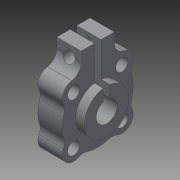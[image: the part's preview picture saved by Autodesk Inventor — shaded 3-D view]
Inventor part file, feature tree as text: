
AUTODESK INVENTOR PART (.ipt)
format: ipt  version: 2014 SP1 (Build 180222100, 222)  size: 246,272 bytes
history: native  units: in
note: dims shown in document units (in); Inventor stores cm internally (conversion verified against a paired STEP export)
features: extrude x3, sketch x3, thread x2, chamfer x1
ambient origin geometry x8: Origin, YZ Plane, XZ Plane, XY Plane, X Axis, Y Axis, Z Axis, Center Point
bodies: Solid1 (feature_tree)
feature tree (9):
  extrude  "Extrusion1"  Depth=0.77in
  extrude  "Extrusion2"  Depth=0.138in
  extrude  "Extrusion3"  Depth=0.275in
  thread  "Thread1"  [1 undecoded]
  thread  "Thread2"  [1 undecoded]
  chamfer  "Chamfer1"  Distance=0.0375in
  sketch  "Sketch1"  dims[d1=0.8in d4=0.77in]
  sketch  "Sketch2"  dims[d6=0.138in d7=0.138in]
  sketch  "Sketch3"  dims[d8=0.138in d9=0.138in d11=0.2362in d12=1.035in d16=0.0375in d17=0.038in d18=0.125in d19=0.125in d20=0.275in d21=0.0in d22=0.5in d23=0.1in d24=0.0in d25=0.138in d26=1.1625in d27=0.0in d28=1.0in d29=0.0in d30=1.0in d31=0.0in d32=0.01in d33=0.125in d34=45.0deg]
note: 2 required parameter values undecoded (feature->parameter linkage not recoverable at this tier; creation-order binding heuristic only, values carry confidence <= 0.55)
